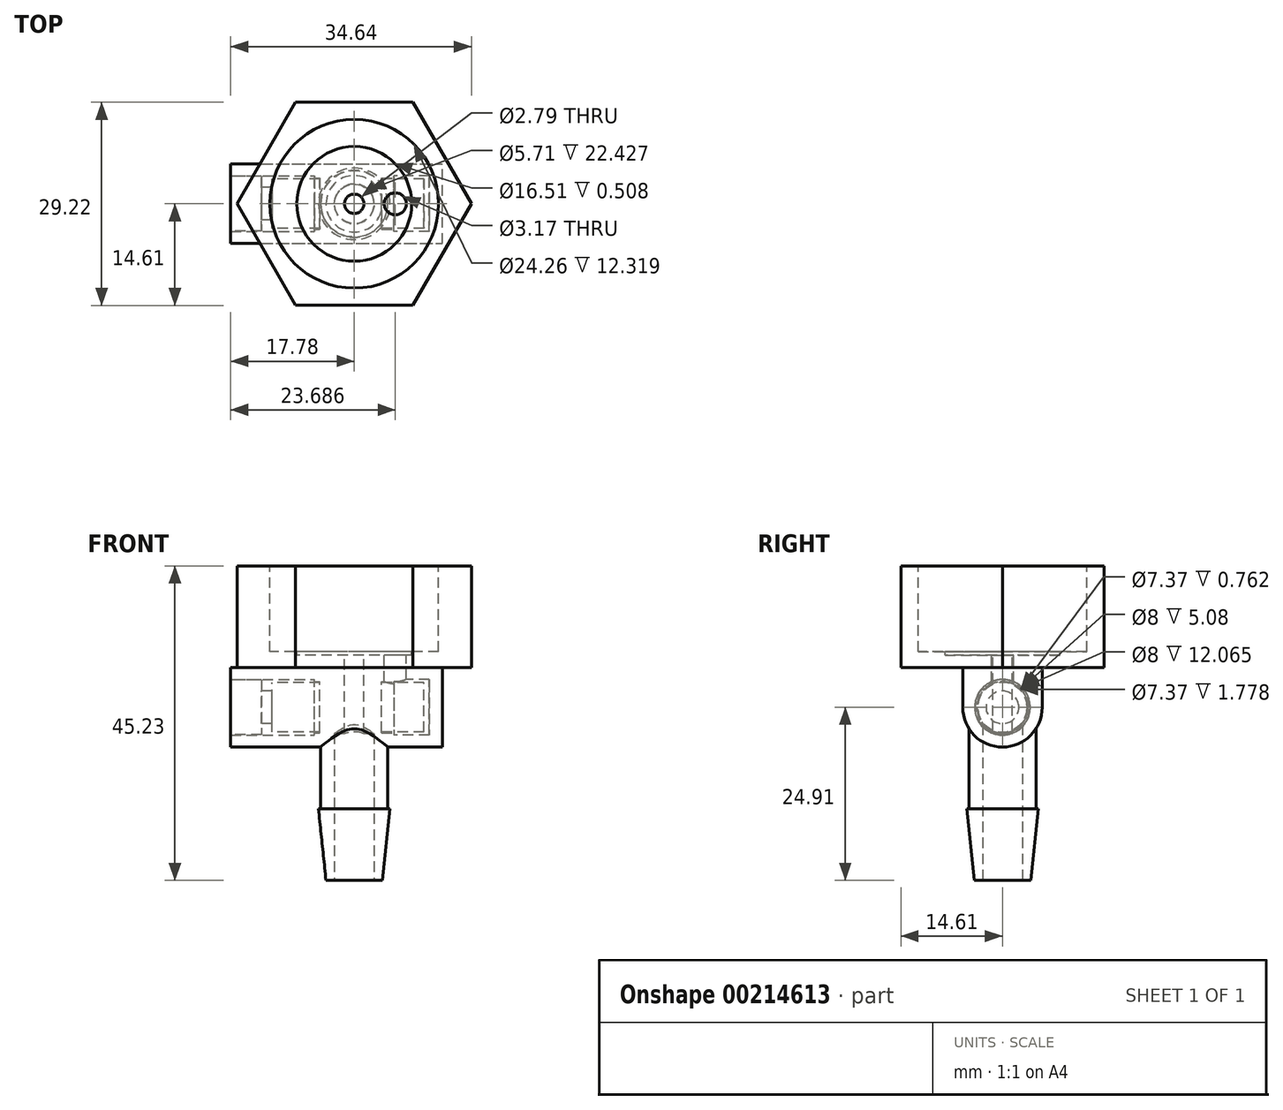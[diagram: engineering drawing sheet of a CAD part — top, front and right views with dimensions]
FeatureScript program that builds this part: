
annotation { "Feature Type Name" : "Feature", "Feature Type Description" : "" }
export const myFeature = defineFeature(function(context is Context, id is Id, definition is map)
    precondition{}
    {
        {
            var Q0;
            Q0=qCreatedBy(makeId("Top.planeOp"),FACE);
            var sketch = newSketch(context, id + "F0", { "sketchPlane" : qUnion([Q0])});
            skCircle(sketch, "E0", {"center": v(0, 0) * mm, "radius": 12.13 * mm});
            skCircle(sketch, "E1", {"center": v(0, 0) * mm, "radius": 13.4 * mm});
            skCircle(sketch, "E2.cCircle", {"center": v(0, 0) * mm, "radius": 14.6 * mm, "construction": true});
            skLineSegment(sketch, "E2.0", {"start": v(16.86, 0) * mm, "end": v(8.43, -14.6) * mm});
            skLineSegment(sketch, "E2.1", {"start": v(8.43, -14.6) * mm, "end": v(-8.43, -14.6) * mm});
            skLineSegment(sketch, "E2.2", {"start": v(-8.43, -14.6) * mm, "end": v(-16.86, 0) * mm});
            skLineSegment(sketch, "E2.3", {"start": v(-16.86, 0) * mm, "end": v(-8.43, 14.6) * mm});
            skLineSegment(sketch, "E2.4", {"start": v(-8.43, 14.6) * mm, "end": v(8.43, 14.6) * mm});
            skLineSegment(sketch, "E2.5", {"start": v(8.43, 14.6) * mm, "end": v(16.86, 0) * mm});
            skPoint(sketch, "E2.0.midPoint", {"position": v(12.65, -7.3) * mm});
            skCircle(sketch, "E3", {"center": v(0, 0) * mm, "radius": 1.4 * mm});
            skCircle(sketch, "E4", {"center": v(5.9, 0) * mm, "radius": 1.59 * mm});
            skCircle(sketch, "E5", {"center": v(0, 0) * mm, "radius": 8.26 * mm});
            skSolve(sketch);
        }
        {
            var Q0;
            Q0=makeQuery(id+"F0.imprint","IMPRINT",FACE,{"disambiguationData":[TD([[makeQuery(id+"F0.imprint","IMPRINT",EDGE,{"derivedFrom":sQuery(id+"F0.wireOp",EDGE,"E1")}),-1.0]])]});
            var Q1;
            Q1=makeQuery(id+"F0.imprint","IMPRINT",FACE,{"disambiguationData":[TD([[makeQuery(id+"F0.imprint","IMPRINT",EDGE,{"derivedFrom":sQuery(id+"F0.wireOp",EDGE,"E0")}),-1.0]])]});
            var Q2;
            Q2=makeQuery(id+"F0.imprint","IMPRINT",FACE,{"disambiguationData":[TD([[makeQuery(id+"F0.imprint","IMPRINT",EDGE,{"derivedFrom":sQuery(id+"F0.wireOp",EDGE,"E0")}),1.0]])]});
            var Q3;
            Q3=makeQuery(id+"F0.imprint","IMPRINT",FACE,{"disambiguationData":[TD([[makeQuery(id+"F0.imprint","IMPRINT",EDGE,{"derivedFrom":sQuery(id+"F0.wireOp",EDGE,"E3")}),-1.0]])]});
            extrude(context, id + "F1", {"entities" : qUnion([Q0, Q1, Q2, Q3]), "oppositeDirection" : true, "depth" : 14.6 * mm});
        }
        {
            var Q0;
            Q0=makeQuery(id+"F0.imprint","IMPRINT",FACE,{"disambiguationData":[TD([[makeQuery(id+"F0.imprint","IMPRINT",EDGE,{"derivedFrom":sQuery(id+"F0.wireOp",EDGE,"E3")}),-1.0]])]});
            extrude(context, id + "F2", {"entities" : qUnion([Q0]), "operationType" : NewBodyOperationType.REMOVE, "oppositeDirection" : true, "depth" : 12.83 * mm});
        }
        {
            var Q0;
            Q0=makeQuery(id+"F0.imprint","IMPRINT",FACE,{"disambiguationData":[TD([[makeQuery(id+"F0.imprint","IMPRINT",EDGE,{"derivedFrom":sQuery(id+"F0.wireOp",EDGE,"E0")}),1.0]])]});
            extrude(context, id + "F3", {"entities" : qUnion([Q0]), "operationType" : NewBodyOperationType.REMOVE, "oppositeDirection" : true, "depth" : 12.32 * mm});
        }
        {
            var Q0;
            Q0=qCreatedBy(makeId("Right.planeOp"),FACE);
            var sketch = newSketch(context, id + "F4", { "sketchPlane" : qUnion([Q0])});
            skLineSegment(sketch, "E6.bottom", {"start": v(-5.72, -14.6) * mm, "end": v(5.71, -14.6) * mm});
            skLineSegment(sketch, "E6.top", {"start": v(-5.72, -26.04) * mm, "end": v(5.71, -26.04) * mm});
            skLineSegment(sketch, "E6.left", {"start": v(-5.72, -14.6) * mm, "end": v(-5.72, -26.04) * mm});
            skLineSegment(sketch, "E6.right", {"start": v(5.71, -14.6) * mm, "end": v(5.71, -26.04) * mm});
            skCircle(sketch, "E7", {"center": v(0, -20.32) * mm, "radius": 3.68 * mm});
            skCircle(sketch, "E8", {"center": v(0, -20.32) * mm, "radius": 4 * mm});
            skArc(sketch, "E9", {"start": v(-5.72, -20.32) * mm, "mid": v(0, -26.04) * mm, "end": v(5.72, -20.32) * mm});
            skSolve(sketch);
        }
        {
            var Q0;
            {var subQ1=sQuery(id+"F4.wireOp",EDGE,"E6.bottom");Q0=makeQuery(id+"F4.imprint","IMPRINT",FACE,{"disambiguationData":[TD([[makeQuery(id+"F4.imprint","IMPRINT",EDGE,{"derivedFrom":subQ1}),-1.0]])]});}
            var Q1;
            Q1=makeQuery(id+"F1.opExtrude","CAP_VERTEX",VERTEX,{"disambiguationData":[OSD([sQuery(id+"F0.wireOp",EDGE,"E2.2"),sQuery(id+"F0.wireOp",EDGE,"E2.3")])],"isStart":false});
            extrude(context, id + "F5", {"entities" : qUnion([Q0]), "operationType" : NewBodyOperationType.ADD, "oppositeDirection" : true, "endBoundEntityVertex" : qUnion([Q1]), "depth" : 17.78 * mm});
        }
        {
            var Q0;
            Q0=makeQuery(id+"F4.imprint","IMPRINT",FACE,{"disambiguationData":[TD([[makeQuery(id+"F4.imprint","IMPRINT",EDGE,{"derivedFrom":sQuery(id+"F4.wireOp",EDGE,"E7")}),-1.0]])]});
            extrude(context, id + "F6", {"entities" : qUnion([Q0]), "operationType" : NewBodyOperationType.ADD, "endBound" : BoundingType.SYMMETRIC, "oppositeDirection" : true, "depth" : 11.43 * mm});
        }
        {
            var Q0;
            {var subQ1=sQuery(id+"F4.wireOp",EDGE,"E6.bottom");Q0=makeQuery(id+"F4.imprint","IMPRINT",FACE,{"disambiguationData":[TD([[makeQuery(id+"F4.imprint","IMPRINT",EDGE,{"derivedFrom":subQ1}),-1.0]])]});}
            extrude(context, id + "F7", {"entities" : qUnion([Q0]), "operationType" : NewBodyOperationType.ADD, "depth" : 12.7 * mm});
        }
        {
            var Q0;
            Q0=makeQuery(id+"F7.opExtrude","CAP_FACE",FACE,{"disambiguationData":[OSD([sQuery(id+"F4.wireOp",EDGE,"E6.bottom"),sQuery(id+"F4.wireOp",EDGE,"E6.left"),sQuery(id+"F4.wireOp",EDGE,"E6.right"),sQuery(id+"F4.wireOp",EDGE,"E8"),sQuery(id+"F4.wireOp",EDGE,"E9")])],"isStart":false});
            var sketch = newSketch(context, id + "F8", { "sketchPlane" : qUnion([Q0])});
            skSolve(sketch);
        }
        {
            var Q0;
            Q0=makeQuery(id+"F8.imprint","IMPRINT",FACE,{"disambiguationData":[TD([[makeQuery(id+"F8.imprint","IMPRINT",EDGE,{"derivedFrom":makeQuery(id+"F7.opExtrude","CAP_EDGE",EDGE,{"disambiguationData":[OSD([sQuery(id+"F4.wireOp",EDGE,"E8")])],"isStart":false})}),1.0]])]});
            extrude(context, id + "F9", {"entities" : qUnion([Q0]), "operationType" : NewBodyOperationType.ADD, "oppositeDirection" : true, "depth" : 1.9 * mm});
        }
        {
            var Q0;
            Q0=makeQuery(id+"F7.boolean.opBoolean","SPLIT",FACE,{"derivedFrom":makeQuery(id+"F7.opExtrude","SWEPT_FACE",FACE,{"disambiguationData":[OSD([sQuery(id+"F4.wireOp",EDGE,"E6.bottom")])]})});
            var Q1;
            {var subQ0=sQuery(id+"F4.wireOp",EDGE,"E6.bottom");var subQ1=sQuery(id+"F0.wireOp",EDGE,"E3");Q1=makeQuery(id+"F7.boolean.opBoolean","MERGE",FACE,{"derivedFrom":[makeQuery(id+"F5.boolean.opBoolean","SPLIT",FACE,{"disambiguationData":[TD([makeQuery(id+"F1.opExtrude","SWEPT_FACE",FACE,{"disambiguationData":[OSD([subQ1])]})])],"derivedFrom":makeQuery(id+"F5.opExtrude","SWEPT_FACE",FACE,{"disambiguationData":[OSD([subQ0])]})}),makeQuery(id+"F7.opExtrude","SWEPT_FACE",FACE,{"disambiguationData":[OSD([subQ0])]})]});}
            extrude(context, id + "F10", {"entities" : qUnion([Q0, Q1]), "operationType" : NewBodyOperationType.REMOVE, "oppositeDirection" : true, "depth" : 7.62 * mm});
        }
        {
            var Q0;
            Q0=makeQuery(id+"F1.opExtrude","CAP_FACE",FACE,{"disambiguationData":[OSD([sQuery(id+"F0.wireOp",EDGE,"E2.0"),sQuery(id+"F0.wireOp",EDGE,"E2.1"),sQuery(id+"F0.wireOp",EDGE,"E2.2"),sQuery(id+"F0.wireOp",EDGE,"E2.3"),sQuery(id+"F0.wireOp",EDGE,"E2.4"),sQuery(id+"F0.wireOp",EDGE,"E2.5"),sQuery(id+"F0.wireOp",EDGE,"E3"),sQuery(id+"F0.wireOp",EDGE,"E4")])],"isStart":true});
            cPlane(context, id + "F11", {"entities" : qUnion([Q0]), "cplaneType" : CPlaneType.OFFSET, "offset" : 26.05 * mm, "oppositeDirection" : true, "width" : 152.4 * mm, "height" : 152.4 * mm});
        }
        {
            var Q0;
            Q0=qCreatedBy(id+"F11.planeOp",FACE);
            var sketch = newSketch(context, id + "F12", { "sketchPlane" : qUnion([Q0])});
            skCircle(sketch, "E10", {"center": v(0, 0) * mm, "radius": 4.83 * mm});
            skSolve(sketch);
        }
        {
            var Q0;
            Q0=makeQuery(id+"F12.imprint","IMPRINT",FACE,{"disambiguationData":[TD([[makeQuery(id+"F12.imprint","IMPRINT",EDGE,{"derivedFrom":sQuery(id+"F12.wireOp",EDGE,"E10")}),1.0]])]});
            extrude(context, id + "F13", {"entities" : qUnion([Q0]), "operationType" : NewBodyOperationType.ADD, "endBound" : BoundingType.UP_TO_NEXT, "depth" : 25.4 * mm});
        }
        {
            var Q0;
            Q0=makeQuery(id+"F13.opExtrude","CAP_FACE",FACE,{"disambiguationData":[OSD([sQuery(id+"F12.wireOp",EDGE,"E10")])],"isStart":true});
            extrude(context, id + "F14", {"entities" : qUnion([Q0]), "operationType" : NewBodyOperationType.ADD, "depth" : 8.9 * mm});
        }
        {
            var Q0;
            Q0=makeQuery(id+"F14.opExtrude","CAP_FACE",FACE,{"disambiguationData":[OSD([sQuery(id+"F12.wireOp",EDGE,"E10")])],"isStart":false});
            var sketch = newSketch(context, id + "F15", { "sketchPlane" : qUnion([Q0])});
            skCircle(sketch, "E11", {"center": v(0, 0) * mm, "radius": 5.14 * mm});
            skSolve(sketch);
        }
        {
            var Q0;
            Q0=makeQuery(id+"F15.imprint","IMPRINT",FACE,{"disambiguationData":[TD([[makeQuery(id+"F15.imprint","IMPRINT",EDGE,{"derivedFrom":sQuery(id+"F15.wireOp",EDGE,"E11")}),1.0]])]});
            var Q1;
            Q1=makeQuery(id+"F15.imprint","IMPRINT",FACE,{"disambiguationData":[TD([[makeQuery(id+"F15.imprint","IMPRINT",EDGE,{"derivedFrom":makeQuery(id+"F14.opExtrude","CAP_EDGE",EDGE,{"disambiguationData":[OSD([sQuery(id+"F12.wireOp",EDGE,"E10")])],"isStart":false})}),-1.0]])]});
            extrude(context, id + "F16", {"entities" : qUnion([Q0, Q1]), "operationType" : NewBodyOperationType.ADD, "depth" : 10.29 * mm, "hasDraft" : true, "draftAngle" : 6 * degree, "draftPullDirection" : true});
        }
        {
            var Q0;
            Q0=makeQuery(id+"F16.opExtrude","CAP_FACE",FACE,{"disambiguationData":[OSD([sQuery(id+"F15.wireOp",EDGE,"E11")])],"isStart":false});
            var sketch = newSketch(context, id + "F17", { "sketchPlane" : qUnion([Q0])});
            skCircle(sketch, "E12", {"center": v(0, 0) * mm, "radius": 2.86 * mm});
            skSolve(sketch);
        }
        {
            var Q0;
            Q0=makeQuery(id+"F17.imprint","IMPRINT",FACE,{"disambiguationData":[TD([[makeQuery(id+"F17.imprint","IMPRINT",EDGE,{"derivedFrom":sQuery(id+"F17.wireOp",EDGE,"E12")}),1.0]])]});
            extrude(context, id + "F18", {"entities" : qUnion([Q0]), "operationType" : NewBodyOperationType.REMOVE, "oppositeDirection" : true, "depth" : 25.4 * mm});
        }
        {
            var Q0;
            Q0=makeQuery(id+"F5.opExtrude","CAP_FACE",FACE,{"disambiguationData":[OSD([sQuery(id+"F4.wireOp",EDGE,"E6.bottom"),sQuery(id+"F4.wireOp",EDGE,"E6.left"),sQuery(id+"F4.wireOp",EDGE,"E6.right"),sQuery(id+"F4.wireOp",EDGE,"E8"),sQuery(id+"F4.wireOp",EDGE,"E9")])],"isStart":false});
            var sketch = newSketch(context, id + "F19", { "sketchPlane" : qUnion([Q0])});
            skCircle(sketch, "E13", {"center": v(0, -20.32) * mm, "radius": 3.94 * mm});
            skSolve(sketch);
        }
        {
            var Q0;
            Q0=makeQuery(id+"F19.imprint","IMPRINT",FACE,{"disambiguationData":[TD([[makeQuery(id+"F19.imprint","IMPRINT",EDGE,{"derivedFrom":sQuery(id+"F19.wireOp",EDGE,"E13")}),1.0]])]});
            extrude(context, id + "F20", {"entities" : qUnion([Q0]), "oppositeDirection" : true, "depth" : 4.44 * mm});
        }
        {
            var Q0;
            Q0=makeQuery(id+"F20.opExtrude","CAP_FACE",FACE,{"disambiguationData":[OSD([sQuery(id+"F19.wireOp",EDGE,"E13")])],"isStart":false});
            var sketch = newSketch(context, id + "F21", { "sketchPlane" : qUnion([Q0])});
            skCircle(sketch, "E14", {"center": v(0, -20.32) * mm, "radius": 2.35 * mm});
            skSolve(sketch);
        }
        {
            var Q0;
            Q0=makeQuery(id+"F21.imprint","IMPRINT",FACE,{"disambiguationData":[TD([[makeQuery(id+"F21.imprint","IMPRINT",EDGE,{"derivedFrom":sQuery(id+"F21.wireOp",EDGE,"E14")}),1.0]])]});
            extrude(context, id + "F22", {"entities" : qUnion([Q0]), "operationType" : NewBodyOperationType.ADD, "depth" : 1.52 * mm});
        }
        {
            var Q0;
            Q0=makeQuery(id+"F22.opExtrude","CAP_FACE",FACE,{"disambiguationData":[OSD([sQuery(id+"F21.wireOp",EDGE,"E14")])],"isStart":false});
            var sketch = newSketch(context, id + "F23", { "sketchPlane" : qUnion([Q0])});
            skCircle(sketch, "E15", {"center": v(0, -20.32) * mm, "radius": 3.56 * mm});
            skSolve(sketch);
        }
        {
            var Q0;
            Q0=makeQuery(id+"F23.imprint","IMPRINT",FACE,{"disambiguationData":[TD([[makeQuery(id+"F23.imprint","IMPRINT",EDGE,{"derivedFrom":sQuery(id+"F23.wireOp",EDGE,"E15")}),1.0]])]});
            var Q1;
            Q1=makeQuery(id+"F23.imprint","IMPRINT",FACE,{"disambiguationData":[TD([[makeQuery(id+"F23.imprint","IMPRINT",EDGE,{"derivedFrom":makeQuery(id+"F22.opExtrude","CAP_EDGE",EDGE,{"disambiguationData":[OSD([sQuery(id+"F21.wireOp",EDGE,"E14")])],"isStart":false})}),1.0]])]});
            extrude(context, id + "F24", {"entities" : qUnion([Q0, Q1]), "operationType" : NewBodyOperationType.ADD, "depth" : 6.86 * mm});
        }
        {
            var Q0;
            Q0=makeQuery(id+"F24.opExtrude","CAP_FACE",FACE,{"disambiguationData":[OSD([sQuery(id+"F23.wireOp",EDGE,"E15")])],"isStart":false});
            var sketch = newSketch(context, id + "F25", { "sketchPlane" : qUnion([Q0])});
            skCircle(sketch, "E16", {"center": v(0, -20.32) * mm, "radius": 3.78 * mm});
            skSolve(sketch);
        }
        {
            var Q0;
            Q0=makeQuery(id+"F25.imprint","IMPRINT",FACE,{"disambiguationData":[TD([[makeQuery(id+"F25.imprint","IMPRINT",EDGE,{"derivedFrom":sQuery(id+"F25.wireOp",EDGE,"E16")}),1.0]])]});
            var Q1;
            Q1=makeQuery(id+"F25.imprint","IMPRINT",FACE,{"disambiguationData":[TD([[makeQuery(id+"F25.imprint","IMPRINT",EDGE,{"derivedFrom":makeQuery(id+"F24.opExtrude","CAP_EDGE",EDGE,{"disambiguationData":[OSD([sQuery(id+"F23.wireOp",EDGE,"E15")])],"isStart":false})}),1.0]])]});
            extrude(context, id + "F26", {"entities" : qUnion([Q0, Q1]), "operationType" : NewBodyOperationType.ADD, "depth" : 8.9 * mm});
        }
        {
            var Q0;
            Q0=makeQuery(id+"F26.opExtrude","CAP_FACE",FACE,{"disambiguationData":[OSD([sQuery(id+"F25.wireOp",EDGE,"E16")])],"isStart":false});
            var sketch = newSketch(context, id + "F27", { "sketchPlane" : qUnion([Q0])});
            skCircle(sketch, "E17.0", {"center": v(0, -20.32) * mm, "radius": 3.56 * mm});
            skSolve(sketch);
        }
        {
            var Q0;
            Q0=makeQuery(id+"F27.imprint","IMPRINT",FACE,{"disambiguationData":[TD([[makeQuery(id+"F27.imprint","IMPRINT",EDGE,{"derivedFrom":sQuery(id+"F27.wireOp",EDGE,"E17.0")}),1.0]])]});
            extrude(context, id + "F28", {"entities" : qUnion([Q0]), "operationType" : NewBodyOperationType.ADD, "depth" : 6.1 * mm});
        }
        {
            var Q0;
            Q0=makeQuery(id+"F2.boolean.opBoolean","COPY",FACE,{"derivedFrom":makeQuery(id+"F2.opExtrude","CAP_FACE",FACE,{"disambiguationData":[OSD([sQuery(id+"F0.wireOp",EDGE,"E3"),sQuery(id+"F0.wireOp",EDGE,"E4"),sQuery(id+"F0.wireOp",EDGE,"E5")])],"isStart":false})});
            var sketch = newSketch(context, id + "F29", { "sketchPlane" : qUnion([Q0])});
            skCircle(sketch, "E18.0", {"center": v(0, 0) * mm, "radius": 1.4 * mm});
            skSolve(sketch);
        }
        {
            var Q0;
            Q0=makeQuery(id+"F29.imprint","IMPRINT",FACE,{"disambiguationData":[TD([[makeQuery(id+"F29.imprint","IMPRINT",EDGE,{"derivedFrom":sQuery(id+"F29.wireOp",EDGE,"E18.0")}),1.0]])]});
            extrude(context, id + "F30", {"entities" : qUnion([Q0]), "operationType" : NewBodyOperationType.REMOVE, "endBound" : BoundingType.THROUGH_ALL, "oppositeDirection" : true, "depth" : 25.4 * mm});
        }
    });
